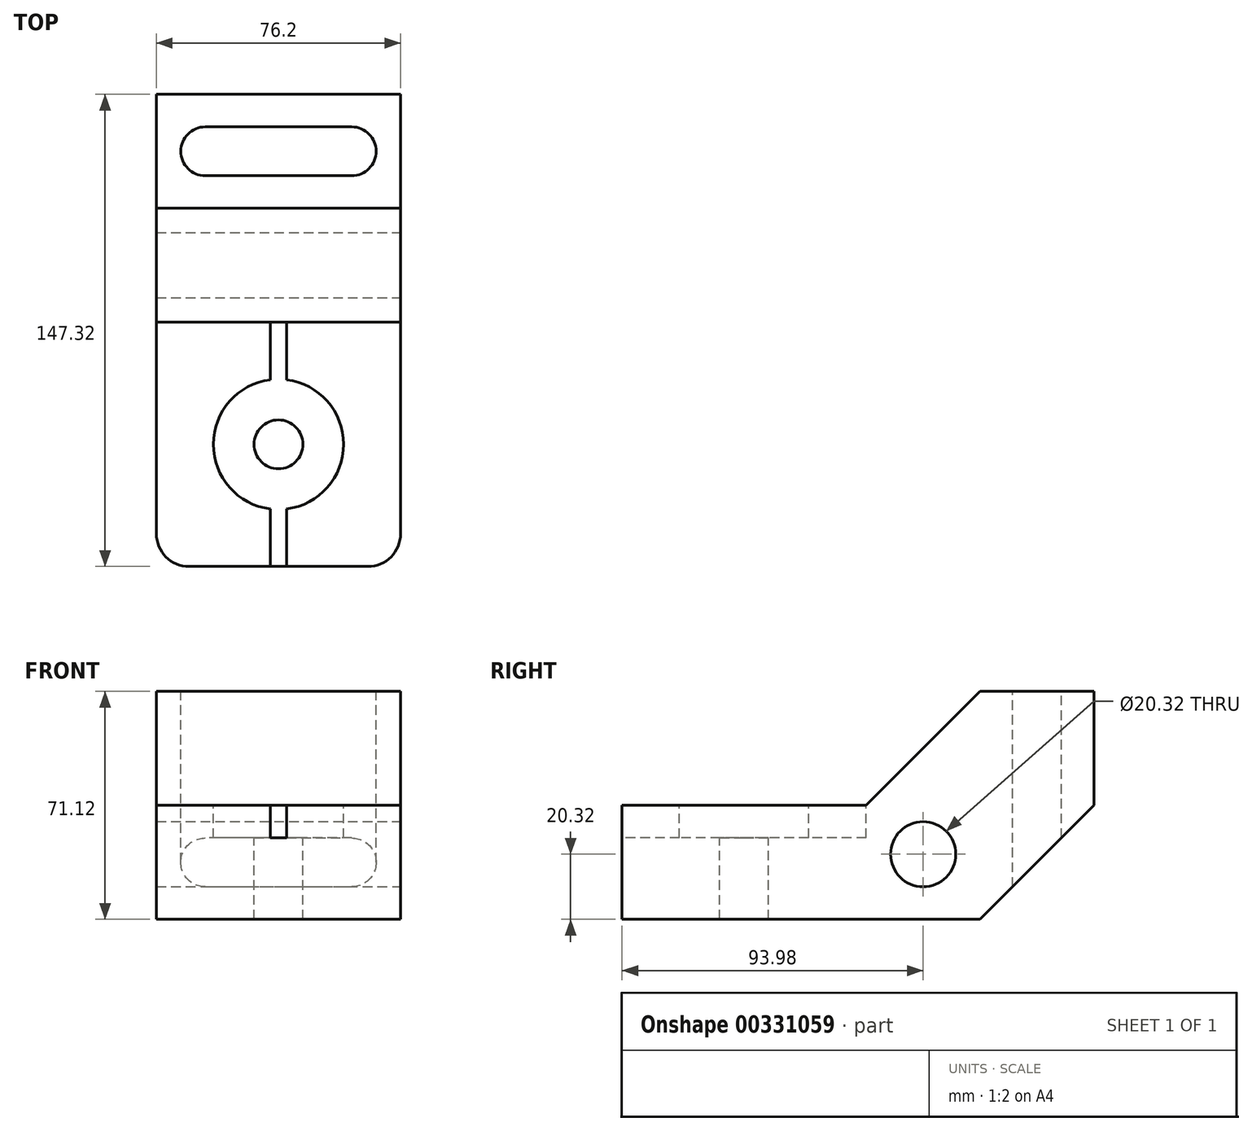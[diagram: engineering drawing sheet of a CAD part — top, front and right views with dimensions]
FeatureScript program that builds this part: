
annotation { "Feature Type Name" : "Feature", "Feature Type Description" : "" }
export const myFeature = defineFeature(function(context is Context, id is Id, definition is map)
    precondition{}
    {
        {
            var Q0;
            Q0=qCreatedBy(makeId("Front.planeOp"),FACE);
            var sketch = newSketch(context, id + "F0", { "sketchPlane" : qUnion([Q0])});
            skLineSegment(sketch, "E0", {"start": v(-38.1, 0) * mm, "end": v(38.1, 0) * mm});
            skLineSegment(sketch, "E1", {"start": v(38.1, 0) * mm, "end": v(38.1, 71.12) * mm});
            skLineSegment(sketch, "E2", {"start": v(38.1, 71.12) * mm, "end": v(-38.1, 71.12) * mm});
            skLineSegment(sketch, "E3", {"start": v(-38.1, 71.12) * mm, "end": v(-38.1, 0) * mm});
            skSolve(sketch);
        }
        {
            var Q0;
            Q0 = qSketchRegion(id + "F0", true);
            extrude(context, id + "F1", {"entities" : qUnion([Q0]), "endBound" : BoundingType.SYMMETRIC, "depth" : 147.32 * mm});
        }
        {
            var Q0;
            Q0=makeQuery(id+"F1.opExtrude","SWEPT_FACE",FACE,{"disambiguationData":[OSD([sQuery(id+"F0.wireOp",EDGE,"E1")])]});
            var sketch = newSketch(context, id + "F2", { "sketchPlane" : qUnion([Q0])});
            skPoint(sketch, "E4.0", {"position": v(-73.66, 71.12) * mm});
            skLineSegment(sketch, "E5", {"start": v(-73.66, 71.12) * mm, "end": v(-73.66, 35.56) * mm});
            skLineSegment(sketch, "E6", {"start": v(-73.66, 35.56) * mm, "end": v(2.54, 35.56) * mm});
            skLineSegment(sketch, "E7", {"start": v(2.54, 35.56) * mm, "end": v(38.1, 71.12) * mm});
            skLineSegment(sketch, "E8", {"start": v(38.1, 71.12) * mm, "end": v(-73.66, 71.12) * mm});
            skPoint(sketch, "E9.0", {"position": v(73.66, 71.12) * mm});
            skPoint(sketch, "E10.0", {"position": v(73.66, 0) * mm});
            skLineSegment(sketch, "E11", {"start": v(73.66, 0) * mm, "end": v(38.1, 0) * mm});
            skLineSegment(sketch, "E12", {"start": v(38.1, 0) * mm, "end": v(73.66, 35.56) * mm});
            skLineSegment(sketch, "E13", {"start": v(73.66, 35.56) * mm, "end": v(73.66, 0) * mm});
            skSolve(sketch);
        }
        {
            var Q0;
            Q0 = qSketchRegion(id + "F2", true);
            extrude(context, id + "F3", {"entities" : qUnion([Q0]), "operationType" : NewBodyOperationType.REMOVE, "endBound" : BoundingType.THROUGH_ALL, "oppositeDirection" : true, "depth" : 25.4 * mm});
        }
        {
            var Q0;
            Q0=makeQuery(id+"F1.opExtrude","SWEPT_FACE",FACE,{"disambiguationData":[OSD([sQuery(id+"F0.wireOp",EDGE,"E1")])]});
            var sketch = newSketch(context, id + "F4", { "sketchPlane" : qUnion([Q0])});
            skPoint(sketch, "E14.0", {"position": v(-73.66, 17.78) * mm});
            skLineSegment(sketch, "E15.0", {"start": v(-73.66, 0) * mm, "end": v(38.1, 0) * mm});
            skCircle(sketch, "E16", {"center": v(20.32, 20.32) * mm, "radius": 10.16 * mm});
            skLineSegment(sketch, "E17.0", {"start": v(73.66, 35.56) * mm, "end": v(73.66, 71.12) * mm});
            skPoint(sketch, "E18.0.6.end.orphan", {"position": v(2.54, 35.56) * mm});
            skPoint(sketch, "E18.0.5.end.orphan", {"position": v(38.1, 71.12) * mm});
            skPoint(sketch, "E18.0.1.start.orphan", {"position": v(-73.66, 35.56) * mm});
            skSolve(sketch);
        }
        {
            var Q0;
            Q0 = qSketchRegion(id + "F4", true);
            extrude(context, id + "F5", {"entities" : qUnion([Q0]), "operationType" : NewBodyOperationType.REMOVE, "endBound" : BoundingType.THROUGH_ALL, "oppositeDirection" : true, "depth" : 25.4 * mm});
        }
        {
            var Q0;
            Q0=makeQuery(id+"F1.opExtrude","SWEPT_FACE",FACE,{"disambiguationData":[OSD([sQuery(id+"F0.wireOp",EDGE,"E2")])]});
            var sketch = newSketch(context, id + "F6", { "sketchPlane" : qUnion([Q0])});
            skLineSegment(sketch, "E19", {"start": v(-22.86, 63.5) * mm, "end": v(22.86, 63.5) * mm});
            skLineSegment(sketch, "E20", {"start": v(22.86, 48.26) * mm, "end": v(-22.86, 48.26) * mm});
            skArc(sketch, "E21", {"start": v(-22.86, 63.5) * mm, "mid": v(-30.48, 55.88) * mm, "end": v(-22.86, 48.26) * mm});
            skArc(sketch, "E22", {"start": v(22.86, 48.26) * mm, "mid": v(30.48, 55.88) * mm, "end": v(22.86, 63.5) * mm});
            skSolve(sketch);
        }
        {
            var Q0;
            Q0 = qSketchRegion(id + "F6", true);
            extrude(context, id + "F7", {"entities" : qUnion([Q0]), "operationType" : NewBodyOperationType.REMOVE, "endBound" : BoundingType.THROUGH_ALL, "oppositeDirection" : true, "depth" : 2.54 * mm});
        }
        {
            var Q0;
            Q0=makeQuery(id+"F3.boolean.opBoolean","COPY",FACE,{"derivedFrom":makeQuery(id+"F3.opExtrude","SWEPT_FACE",FACE,{"disambiguationData":[OSD([sQuery(id+"F2.wireOp",EDGE,"E6")])]})});
            var sketch = newSketch(context, id + "F8", { "sketchPlane" : qUnion([Q0])});
            skPoint(sketch, "E23", {"position": v(0, -35.56) * mm});
            skSolve(sketch);
        }
        {
            var Q0;
            Q0=sQuery(id+"F8.wireOp",VERTEX,"E23");
            var Q1;
            Q1=makeQuery(id+"F1.opExtrude","SWEPT_BODY",BODY,{"disambiguationData":[OSD([sQuery(id+"F0.wireOp",EDGE,"E0"),sQuery(id+"F0.wireOp",EDGE,"E1"),sQuery(id+"F0.wireOp",EDGE,"E2"),sQuery(id+"F0.wireOp",EDGE,"E3")])]});
            hole(context, id + "F9", {"style" : HoleStyle.C_BORE, "endStyle" : HoleEndStyle.THROUGH, "holeDiameter" : 15.24 * mm, "cBoreDiameter" : 40.64 * mm, "cBoreDepth" : 10.16 * mm, "tappedDepth" : 12.7 * mm, "tapClearance" : 3, "locations" : qUnion([Q0]), "scope" : qUnion([Q1])});
        }
        {
            var Q0;
            Q0=makeQuery(id+"F1.opExtrude","CAP_FACE",FACE,{"disambiguationData":[OSD([sQuery(id+"F0.wireOp",EDGE,"E0"),sQuery(id+"F0.wireOp",EDGE,"E1"),sQuery(id+"F0.wireOp",EDGE,"E2"),sQuery(id+"F0.wireOp",EDGE,"E3")])],"isStart":false});
            var sketch = newSketch(context, id + "F10", { "sketchPlane" : qUnion([Q0])});
            skLineSegment(sketch, "E24", {"start": v(-2.54, 35.56) * mm, "end": v(-2.54, 25.4) * mm});
            skLineSegment(sketch, "E25", {"start": v(-2.54, 25.4) * mm, "end": v(2.54, 25.4) * mm});
            skLineSegment(sketch, "E26", {"start": v(2.54, 25.4) * mm, "end": v(2.54, 35.56) * mm});
            skLineSegment(sketch, "E27", {"start": v(2.54, 35.56) * mm, "end": v(-2.54, 35.56) * mm});
            skLineSegment(sketch, "E28", {"start": v(0, 25.4) * mm, "end": v(0, 0) * mm, "construction": true});
            skSolve(sketch);
        }
        {
            var Q0;
            Q0 = qSketchRegion(id + "F10", true);
            extrude(context, id + "F11", {"entities" : qUnion([Q0]), "operationType" : NewBodyOperationType.REMOVE, "oppositeDirection" : true, "depth" : 76.2 * mm});
        }
        {
            var Q0;
            Q0=makeQuery(id+"F1.opExtrude","CAP_EDGE",EDGE,{"disambiguationData":[OSD([sQuery(id+"F0.wireOp",EDGE,"E1")])],"isStart":false});
            var Q1;
            Q1=makeQuery(id+"F1.opExtrude","CAP_EDGE",EDGE,{"disambiguationData":[OSD([sQuery(id+"F0.wireOp",EDGE,"E3")])],"isStart":false});
            fillet(context, id + "F12", {"entities" : qUnion([Q0, Q1]), "radius" : 10.16 * mm, "tangentPropagation" : true, "allowEdgeOverflow" : false});
        }
    });
